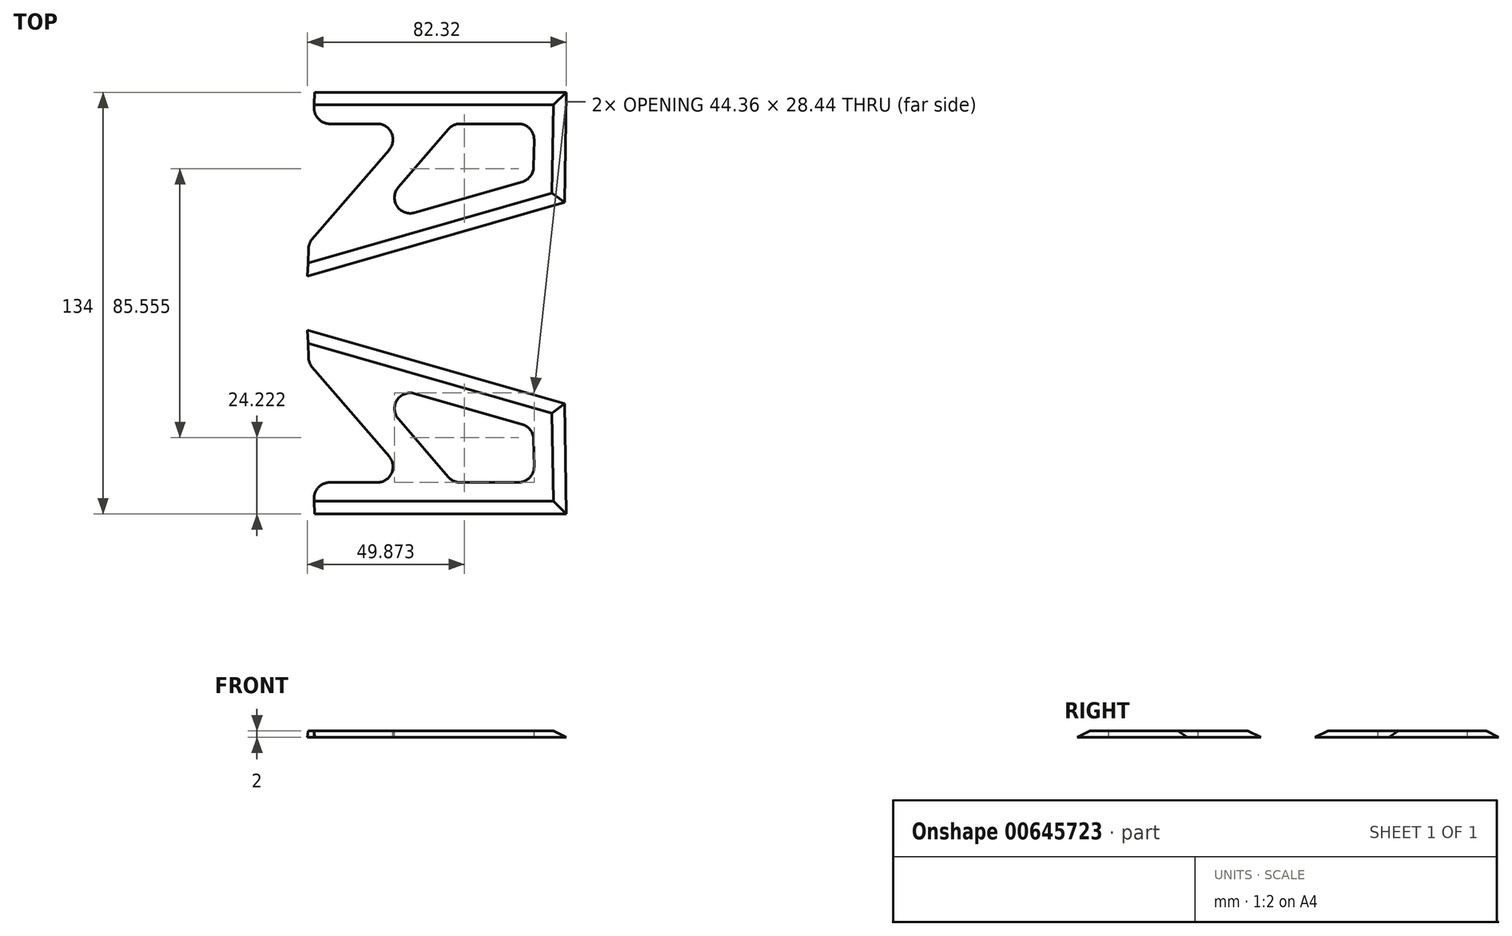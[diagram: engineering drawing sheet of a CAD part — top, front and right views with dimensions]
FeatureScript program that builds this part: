
annotation { "Feature Type Name" : "Feature", "Feature Type Description" : "" }
export const myFeature = defineFeature(function(context is Context, id is Id, definition is map)
    precondition{}
    {
        {
            var Q0;
            Q0=qCreatedBy(makeId("Front.planeOp"),FACE);
            var sketch = newSketch(context, id + "F0", { "sketchPlane" : qUnion([Q0])});
            skLineSegment(sketch, "E0", {"start": v(-29.78, 27.84) * mm, "end": v(50.22, 27.84) * mm});
            skLineSegment(sketch, "E1", {"start": v(50.22, 27.84) * mm, "end": v(49.6, -7.16) * mm});
            skLineSegment(sketch, "E2", {"start": v(49.6, -7.16) * mm, "end": v(-32.1, -30.59) * mm});
            skLineSegment(sketch, "E3", {"start": v(-29.78, 27.84) * mm, "end": v(-29.97, 23.03) * mm});
            skLineSegment(sketch, "E4.0", {"start": v(36.18, -0.6) * mm, "end": v(1.96, -10.42) * mm});
            skLineSegment(sketch, "E4.1", {"start": v(39.95, 12.75) * mm, "end": v(39.8, 4.11) * mm});
            skLineSegment(sketch, "E4.2", {"start": v(-24.98, 17.84) * mm, "end": v(-9.92, 17.84) * mm});
            skLineSegment(sketch, "E5", {"start": v(-30.54, -18.74) * mm, "end": v(-6.14, 9.57) * mm});
            skLineSegment(sketch, "E6.0", {"start": v(-3.2, -2.35) * mm, "end": v(12.7, 16.1) * mm});
            skLineSegment(sketch, "E7.trimOffspring", {"start": v(-31.75, -21.8) * mm, "end": v(-32.1, -30.59) * mm});
            skLineSegment(sketch, "E8.trimOffspring", {"start": v(16.48, 17.84) * mm, "end": v(34.95, 17.84) * mm});
            skPoint(sketch, "E9.visualSharp", {"position": v(0.99, 17.84) * mm});
            skArc(sketch, "E9.filletArc", {"start": v(-6.14, 9.57) * mm, "mid": v(-5.38, 14.92) * mm, "end": v(-9.92, 17.84) * mm});
            skPoint(sketch, "E10.visualSharp", {"position": v(14.2, 17.84) * mm});
            skArc(sketch, "E10.filletArc", {"start": v(16.48, 17.84) * mm, "mid": v(14.4, 17.38) * mm, "end": v(12.7, 16.1) * mm});
            skPoint(sketch, "E11.visualSharp", {"position": v(-14.14, -15.04) * mm});
            skArc(sketch, "E11.filletArc", {"start": v(-3.2, -2.35) * mm, "mid": v(-3.63, -8.3) * mm, "end": v(1.96, -10.42) * mm});
            skPoint(sketch, "E12.visualSharp", {"position": v(39.74, 0.41) * mm});
            skArc(sketch, "E12.filletArc", {"start": v(36.18, -0.6) * mm, "mid": v(38.77, 1.16) * mm, "end": v(39.8, 4.11) * mm});
            skPoint(sketch, "E13.visualSharp", {"position": v(40.04, 17.84) * mm});
            skArc(sketch, "E13.filletArc", {"start": v(39.95, 12.75) * mm, "mid": v(38.52, 16.34) * mm, "end": v(34.95, 17.84) * mm});
            skPoint(sketch, "E14.visualSharp", {"position": v(-31.68, -20.06) * mm});
            skArc(sketch, "E14.filletArc", {"start": v(-30.54, -18.74) * mm, "mid": v(-31.4, -20.17) * mm, "end": v(-31.75, -21.8) * mm});
            skPoint(sketch, "E15.visualSharp", {"position": v(-30.18, 17.84) * mm});
            skArc(sketch, "E15.filletArc", {"start": v(-29.97, 23.03) * mm, "mid": v(-28.58, 19.37) * mm, "end": v(-24.98, 17.84) * mm});
            skSolve(sketch);
        }
        {
            var Q0;
            Q0=makeQuery(id+"F0.imprint","IMPRINT",FACE,{"disambiguationData":[TD([[makeQuery(id+"F0.imprint","IMPRINT",EDGE,{"derivedFrom":sQuery(id+"F0.wireOp",EDGE,"E0")}),-1.0]])]});
            extrude(context, id + "F1", {"entities" : qUnion([Q0]), "depth" : 2 * mm, "offsetDistance" : 25 * mm});
        }
        {
            var Q0;
            Q0=makeQuery(id+"F1.opExtrude","CAP_EDGE",EDGE,{"disambiguationData":[OSD([sQuery(id+"F0.wireOp",EDGE,"E0")])],"isStart":true});
            var Q1;
            Q1=makeQuery(id+"F1.opExtrude","CAP_EDGE",EDGE,{"disambiguationData":[OSD([sQuery(id+"F0.wireOp",EDGE,"E1")])],"isStart":true});
            var Q2;
            Q2=makeQuery(id+"F1.opExtrude","CAP_EDGE",EDGE,{"disambiguationData":[OSD([sQuery(id+"F0.wireOp",EDGE,"E2")])],"isStart":true});
            chamfer(context, id + "F2", {"entities" : qUnion([Q0, Q1, Q2]), "chamferType" : ChamferType.TWO_OFFSETS, "width1" : 4 * mm, "oppositeDirection" : false, "width2" : 2 * mm, "tangentPropagation" : true});
        }
        {
            var Q0;
            Q0=makeQuery(id+"F1.opExtrude","CAP_FACE",FACE,{"disambiguationData":[OSD([sQuery(id+"F0.wireOp",EDGE,"E0"),sQuery(id+"F0.wireOp",EDGE,"E1"),sQuery(id+"F0.wireOp",EDGE,"E2"),sQuery(id+"F0.wireOp",EDGE,"E3"),sQuery(id+"F0.wireOp",EDGE,"E4.0"),sQuery(id+"F0.wireOp",EDGE,"E4.1"),sQuery(id+"F0.wireOp",EDGE,"E4.2"),sQuery(id+"F0.wireOp",EDGE,"E5"),sQuery(id+"F0.wireOp",EDGE,"E6.0"),sQuery(id+"F0.wireOp",EDGE,"E7.trimOffspring"),sQuery(id+"F0.wireOp",EDGE,"E8.trimOffspring"),sQuery(id+"F0.wireOp",EDGE,"E9.filletArc"),sQuery(id+"F0.wireOp",EDGE,"E10.filletArc"),sQuery(id+"F0.wireOp",EDGE,"E11.filletArc"),sQuery(id+"F0.wireOp",EDGE,"E12.filletArc"),sQuery(id+"F0.wireOp",EDGE,"E13.filletArc"),sQuery(id+"F0.wireOp",EDGE,"E14.filletArc"),sQuery(id+"F0.wireOp",EDGE,"E15.filletArc")])],"isStart":true});
            cPlane(context, id + "F3", {"entities" : qUnion([Q0]), "cplaneType" : CPlaneType.OFFSET, "offset" : 15 * mm, "width" : 150 * mm, "height" : 150 * mm});
        }
        {
            var Q0;
            Q0=makeQuery(id+"F1.opExtrude","SWEPT_BODY",BODY,{"disambiguationData":[OSD([sQuery(id+"F0.wireOp",EDGE,"E0"),sQuery(id+"F0.wireOp",EDGE,"E1"),sQuery(id+"F0.wireOp",EDGE,"E2"),sQuery(id+"F0.wireOp",EDGE,"E3"),sQuery(id+"F0.wireOp",EDGE,"E4.0"),sQuery(id+"F0.wireOp",EDGE,"E4.1"),sQuery(id+"F0.wireOp",EDGE,"E4.2"),sQuery(id+"F0.wireOp",EDGE,"E5"),sQuery(id+"F0.wireOp",EDGE,"E6.0"),sQuery(id+"F0.wireOp",EDGE,"E7.trimOffspring"),sQuery(id+"F0.wireOp",EDGE,"E8.trimOffspring"),sQuery(id+"F0.wireOp",EDGE,"E9.filletArc"),sQuery(id+"F0.wireOp",EDGE,"E10.filletArc"),sQuery(id+"F0.wireOp",EDGE,"E11.filletArc"),sQuery(id+"F0.wireOp",EDGE,"E12.filletArc"),sQuery(id+"F0.wireOp",EDGE,"E13.filletArc"),sQuery(id+"F0.wireOp",EDGE,"E14.filletArc"),sQuery(id+"F0.wireOp",EDGE,"E15.filletArc")])]});
            var Q1;
            {var subQ0=sQuery(id+"F0.wireOp",EDGE,"E0");Q1=makeQuery(id+"F2.opChamfer","BLEND_EDGE",EDGE,{"blendedFrom":[makeQuery(id+"F1.opExtrude","CAP_EDGE",EDGE,{"disambiguationData":[OSD([subQ0])],"isStart":true}),makeQuery(id+"F1.opExtrude","CAP_FACE",FACE,{"disambiguationData":[OSD([subQ0,sQuery(id+"F0.wireOp",EDGE,"E1"),sQuery(id+"F0.wireOp",EDGE,"E2"),sQuery(id+"F0.wireOp",EDGE,"E3"),sQuery(id+"F0.wireOp",EDGE,"E4.0"),sQuery(id+"F0.wireOp",EDGE,"E4.1"),sQuery(id+"F0.wireOp",EDGE,"E4.2"),sQuery(id+"F0.wireOp",EDGE,"E5"),sQuery(id+"F0.wireOp",EDGE,"E6.0"),sQuery(id+"F0.wireOp",EDGE,"E7.trimOffspring"),sQuery(id+"F0.wireOp",EDGE,"E8.trimOffspring"),sQuery(id+"F0.wireOp",EDGE,"E9.filletArc"),sQuery(id+"F0.wireOp",EDGE,"E10.filletArc"),sQuery(id+"F0.wireOp",EDGE,"E11.filletArc"),sQuery(id+"F0.wireOp",EDGE,"E12.filletArc"),sQuery(id+"F0.wireOp",EDGE,"E13.filletArc"),sQuery(id+"F0.wireOp",EDGE,"E14.filletArc"),sQuery(id+"F0.wireOp",EDGE,"E15.filletArc")])],"isStart":false})],"blendedInto":[makeQuery(id+"F1.opExtrude","CAP_FACE",FACE,{"disambiguationData":[OSD([subQ0,sQuery(id+"F0.wireOp",EDGE,"E1"),sQuery(id+"F0.wireOp",EDGE,"E2"),sQuery(id+"F0.wireOp",EDGE,"E3"),sQuery(id+"F0.wireOp",EDGE,"E4.0"),sQuery(id+"F0.wireOp",EDGE,"E4.1"),sQuery(id+"F0.wireOp",EDGE,"E4.2"),sQuery(id+"F0.wireOp",EDGE,"E5"),sQuery(id+"F0.wireOp",EDGE,"E6.0"),sQuery(id+"F0.wireOp",EDGE,"E7.trimOffspring"),sQuery(id+"F0.wireOp",EDGE,"E8.trimOffspring"),sQuery(id+"F0.wireOp",EDGE,"E9.filletArc"),sQuery(id+"F0.wireOp",EDGE,"E10.filletArc"),sQuery(id+"F0.wireOp",EDGE,"E11.filletArc"),sQuery(id+"F0.wireOp",EDGE,"E12.filletArc"),sQuery(id+"F0.wireOp",EDGE,"E13.filletArc"),sQuery(id+"F0.wireOp",EDGE,"E14.filletArc"),sQuery(id+"F0.wireOp",EDGE,"E15.filletArc")])],"isStart":false})]});}
            transform(context, id + "F4", {"entities" : qUnion([Q0]), "transformType" : TransformType.ROTATION, "transformAxis" : qUnion([Q1]), "angle" : 90 * degree, "makeCopy" : false});
        }
        {
            var Q0;
            Q0=makeQuery(id+"F1.opExtrude","SWEPT_BODY",BODY,{"disambiguationData":[OSD([sQuery(id+"F0.wireOp",EDGE,"E0"),sQuery(id+"F0.wireOp",EDGE,"E1"),sQuery(id+"F0.wireOp",EDGE,"E2"),sQuery(id+"F0.wireOp",EDGE,"E3"),sQuery(id+"F0.wireOp",EDGE,"E4.0"),sQuery(id+"F0.wireOp",EDGE,"E4.1"),sQuery(id+"F0.wireOp",EDGE,"E4.2"),sQuery(id+"F0.wireOp",EDGE,"E5"),sQuery(id+"F0.wireOp",EDGE,"E6.0"),sQuery(id+"F0.wireOp",EDGE,"E7.trimOffspring"),sQuery(id+"F0.wireOp",EDGE,"E8.trimOffspring"),sQuery(id+"F0.wireOp",EDGE,"E9.filletArc"),sQuery(id+"F0.wireOp",EDGE,"E10.filletArc"),sQuery(id+"F0.wireOp",EDGE,"E11.filletArc"),sQuery(id+"F0.wireOp",EDGE,"E12.filletArc"),sQuery(id+"F0.wireOp",EDGE,"E13.filletArc"),sQuery(id+"F0.wireOp",EDGE,"E14.filletArc"),sQuery(id+"F0.wireOp",EDGE,"E15.filletArc")])]});
            var Q1;
            Q1=qCreatedBy(makeId("Front.planeOp"),FACE);
            transform(context, id + "F5", {"entities" : qUnion([Q0]), "transformType" : TransformType.TRANSLATION_DISTANCE, "transformDirection" : qUnion([Q1]), "distance" : 50 * mm, "makeCopy" : false});
        }
        {
            var Q0;
            Q0=makeQuery(id+"F1.opExtrude","SWEPT_BODY",BODY,{"disambiguationData":[OSD([sQuery(id+"F0.wireOp",EDGE,"E0"),sQuery(id+"F0.wireOp",EDGE,"E1"),sQuery(id+"F0.wireOp",EDGE,"E2"),sQuery(id+"F0.wireOp",EDGE,"E3"),sQuery(id+"F0.wireOp",EDGE,"E4.0"),sQuery(id+"F0.wireOp",EDGE,"E4.1"),sQuery(id+"F0.wireOp",EDGE,"E4.2"),sQuery(id+"F0.wireOp",EDGE,"E5"),sQuery(id+"F0.wireOp",EDGE,"E6.0"),sQuery(id+"F0.wireOp",EDGE,"E7.trimOffspring"),sQuery(id+"F0.wireOp",EDGE,"E8.trimOffspring"),sQuery(id+"F0.wireOp",EDGE,"E9.filletArc"),sQuery(id+"F0.wireOp",EDGE,"E10.filletArc"),sQuery(id+"F0.wireOp",EDGE,"E11.filletArc"),sQuery(id+"F0.wireOp",EDGE,"E12.filletArc"),sQuery(id+"F0.wireOp",EDGE,"E13.filletArc"),sQuery(id+"F0.wireOp",EDGE,"E14.filletArc"),sQuery(id+"F0.wireOp",EDGE,"E15.filletArc")])]});
            var Q1;
            Q1=qCreatedBy(id+"F3.planeOp",FACE);
            mirror(context, id + "F6", {"entities" : qUnion([Q0]), "mirrorPlane" : qUnion([Q1])});
        }
    });
